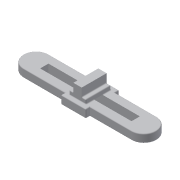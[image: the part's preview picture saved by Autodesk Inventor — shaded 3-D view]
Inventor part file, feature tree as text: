
AUTODESK INVENTOR PART (.ipt)
format: ipt  version: 2014 (Build 180170000, 170)  size: 198,144 bytes
history: native  units: mm
features: fillet x3, extrude x2, sketch x2
ambient origin geometry x8: Origin, YZ Plane, XZ Plane, XY Plane, X Axis, Y Axis, Z Axis, Center Point
bodies: Solid1 (feature_tree)
feature tree (7):
  extrude  "Extrusion1"  Depth=30.0mm
  extrude  "Extrusion2"  Depth=10.0mm
  fillet  "Fillet1"  Radius=220.0mm
  fillet  "Fillet2"  Radius=20.0mm
  fillet  "Fillet3"  Radius=20.0mm
  sketch  "Sketch1"  dims[d0=260.0mm d1=30.0mm]
  sketch  "Sketch2"  dims[d2=60.0mm d3=10.0mm d4=220.0mm d5=20.0mm d6=20.0mm d7=0.0mm d8=40.0mm d9=10.0mm d10=10.0mm d11=20.0mm d12=60.0mm d13=0.0mm d14=2.0mm d15=2.0mm d16=2.0mm]
